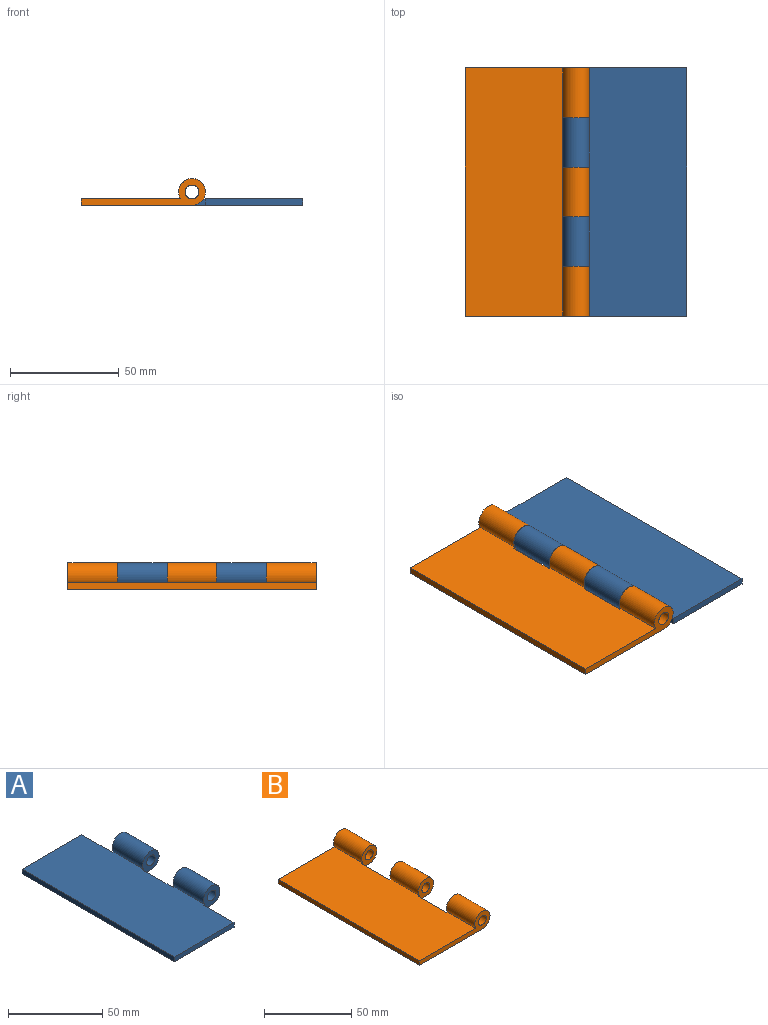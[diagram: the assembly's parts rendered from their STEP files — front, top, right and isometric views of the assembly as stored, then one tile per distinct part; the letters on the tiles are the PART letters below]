
ASSEMBLY  parts=2 mates=1
PART A: 16 faces, bbox 57.2x114.3x12.3 mm
  f0: plane 114.3x51mm, normal (0,0,-1), area 5407.2mm2, adj f1,f2,f4,f5,f6,f7,f8,f9
  f1: cylinder r=6.15mm len=22.86mm, axis (0,1,0), area 737mm2, adj f0,f3,f8,f13
  f2: cylinder r=6.15mm len=22.86mm, axis (0,1,0), area 737mm2, adj f0,f3,f7,f11
  f3: plane 114.3x45.69mm, normal (0,0,1), area 5164.4mm2, adj f1,f2,f4,f5,f6,f7,f8,f9
  f4: plane 114.3x3.05mm, normal (-1,0,0), area 348.4mm2, adj f0,f3,f5,f6
  f5: plane 44.85x3.05mm, normal (0,-1,0), area 136.7mm2, adj f0,f3,f4,f12
  f6: plane 44.85x3.05mm, normal (0,1,0), area 136.7mm2, adj f0,f3,f4,f14
  f7: plane 12.3x12.3mm, normal (0,1,0), area 94.5mm2, adj f0,f2,f3,f9,f10
  f8: plane 12.3x12.3mm, normal (0,-1,0), area 94.5mm2, adj f0,f1,f3,f9,f15
  f9: plane 22.86x3.05mm, normal (1,0,0), area 69.7mm2, adj f0,f3,f7,f8
  f10: cylinder r=3.17mm len=22.86mm, axis (0,1,0), area 456mm2, adj f7,f11
  f11: plane 12.3x12.3mm, normal (0,-1,0), area 94.5mm2, adj f0,f2,f3,f10,f12
  f12: plane 22.86x3.05mm, normal (1,0,0), area 69.7mm2, adj f0,f3,f5,f11
  f13: plane 12.3x12.3mm, normal (0,1,0), area 94.5mm2, adj f0,f1,f3,f14,f15
  f14: plane 22.86x3.05mm, normal (1,0,0), area 69.7mm2, adj f0,f3,f6,f13
  f15: cylinder r=3.17mm len=22.86mm, axis (0,1,0), area 456mm2, adj f8,f13
PART B: 17 faces, bbox 57.2x114.3x12.3 mm
  f0: cylinder r=6.15mm len=22.86mm, axis (0,1,0), area 737mm2, adj f3,f6,f8,f14
  f1: cylinder r=6.15mm len=22.86mm, axis (0,1,0), area 737mm2, adj f3,f6,f10,f15
  f2: cylinder r=6.15mm len=22.86mm, axis (0,1,0), area 737mm2, adj f3,f6,f9,f11
  f3: plane 114.3x45.69mm, normal (0,0,1), area 5183.6mm2, adj f0,f1,f2,f5,f8,f9,f10,f11
  f4: cylinder r=3.17mm len=22.86mm, axis (0,1,0), area 456mm2, adj f8,f14
  f5: plane 114.3x3.05mm, normal (-1,0,0), area 348.4mm2, adj f3,f6,f8,f9
  f6: plane 114.3x51mm, normal (0,0,-1), area 5547.9mm2, adj f0,f1,f2,f5,f8,f9,f10,f11
  f7: cylinder r=3.17mm len=22.86mm, axis (0,1,0), area 456mm2, adj f9,f11
  f8: plane 57.15x12.3mm, normal (0,-1,0), area 231.2mm2, adj f0,f3,f4,f5,f6
  f9: plane 57.15x12.3mm, normal (0,1,0), area 231.2mm2, adj f2,f3,f5,f6,f7
  f10: plane 12.3x12.3mm, normal (0,1,0), area 94.5mm2, adj f1,f3,f6,f12,f13
  f11: plane 12.3x12.3mm, normal (0,-1,0), area 94.5mm2, adj f2,f3,f6,f7,f12
  f12: plane 22.86x3.05mm, normal (1,0,0), area 69.7mm2, adj f3,f6,f10,f11
  f13: cylinder r=3.17mm len=22.86mm, axis (0,1,0), area 456mm2, adj f10,f15
  f14: plane 12.3x12.3mm, normal (0,1,0), area 94.5mm2, adj f0,f3,f4,f6,f16
  f15: plane 12.3x12.3mm, normal (0,-1,0), area 94.5mm2, adj f1,f3,f6,f13,f16
  f16: plane 22.86x3.05mm, normal (1,0,0), area 69.7mm2, adj f3,f6,f14,f15
PLACE A rot(axis=(0,0,-1),180deg) t=(80.51,-71.14,-6.35)mm
PLACE B t=(-21.49,43.16,-6.35)mm
MATE cylindrical A.f1 <-> B.f0  axis (0,1,0) through (29.51,20.3,-0.2)mm
